# Revit family: PRD_AR_WllMntdBbTps_F5SSelfClosingMixer_F5SM1012
name_source: partatom
category: Plumbing Fixtures
units: mm (PartAtom-declared; Revit-internal decimal feet)

## family parameters
Cut with Voids When Loaded = No
Enable Cutting in Views = Yes
Host = Face
Maintain Annotation Orientation = No
OmniClass Number = 23.45.55.14
OmniClass Title = Single Faucets
Part Type = Normal
Room Calculation Point = No
Round Connector Dimension = Use Diameter
Shared = No

## types (1)
- F5SM1012
    AccentColour = none
    AdjustableFlowTime = Yes
    AssetType = Fixed
    BIMObjectName = PRD_AR_WallMountedBibTaps_F5SSelfClosingMixer_F5SM1012
    BasicColour = chrome-look (glossy)
    BodyMaterial = PRD_AR_PolishedChromium_PlatedBrass
    CW Connection = Yes
    CWFU = 0
    CalculationFlowRateColdWater = 0.07 l/s
    CalculationFlowRateHotWater = 0.07 l/s
    Category = Pr_40_20_87_93, Wall-mounted bib taps
    CloseOffRating = 0.0 Pa
    Color = chrome-look (glossy)
    DN = 15 mm  [stored 0.0492126 ft]
    Default Elevation = 1219 mm
    Depressurised = No
    Description = F5S-Mix self-closing wall-mounted mixer DN 15 as single mixer with angled outlet, for sanitary facilities, for concealed mounting. Especially suitable for facilities at risk of vandalism. FRAMIC self-closing mixer cartridge, hydraulically controlled, low-maintenance and stagnation-free, with ceramic disc technology, self-closing, flow pressure-independent due to medium separated design. Stepless adjustment of flow duration. With adjustable and turn-proof temperature stop with backflow preventers and strainers. For connection to hot and cold water. All-metal construction, polished, chromium-plated brass. Anti-theft aerator with integrated flow regulator 6.0 l/min. Connecting flange with overlapping wall bushings for wall thicknesses from 50 to 240 mm.
    DiameterNominal = DN 15
    Export Type to IFC As = IfcValveType
    FaucetFunction = MIXED
    FaucetOperation = SELFCLOSING
    FaucetTopDescription = Top section, ceramic
    FaucetType = BIB
    Features = For connection to hot and cold water. All-metal construction, polished, chromium-plated brass. Anti-theft aerator with integrated flow regulator 6.0 l/min. Other wall thicknesses on request.
    Finish = chromed
    FlowCoefficient = 0
    FlowColdWater = 0.1 L/s
    FlowHotWater = 0.1 L/s
    FunctionalPrinciple = hydraulic self-closing
    HW Connection = Yes
    HWFU = 0
    HygieneFlushing = No
    IfcExportAs = IfcValveType
    IfcExportType = FAUCET
    InletSize = G 1/2 B
    LockingMechanism = Top section, ceramic
    Manufacturer = KWC Group Management AG
    ManufacturerName = KWC Group Management AG
    ManufacturerURL = www.kwc-professional.com
    Material = polished, chromium-plated brass
    MaterialFitting = brass-look
    MaximumFlowTime = 35 Seconds
    MinimumFlowPressure = 1 bar
    MinimumFlowTime = 5 Seconds
    Model = F5SM1012
    ModelNumber = 2030071618
    ModelReference = F5SM1012
    NBSDescription = Taps and water supply fittings for sinks
    NBSReference = 45-35-70/345
    Name = F5S Self-closing mixer F5SM1012
    NominalDepth = 232 mm  [stored 0.761155 ft]
    NominalHeight = 0 mm  [stored 0 ft]
    NominalWidth = 71 mm  [stored 0.23294 ft]
    ProductInformation = http://pim.kwc.com
    Protective Shutdown = No
    Size = 15
    SoundInsulation = No
    Spout = fixed
    SpoutProjection = 170 mm
    Status = New
    SurfaceFinishFitting = chromed
    SurfaceTreatmentFitting = polished
    TemperatureLimit = Yes
    TestPressure = 0.0 Pa
    ThermalDisinfection = No
    Type IFC Predefined Type = FAUCET
    TypeOfMixing = Yes
    TypeOfMounting = concealed
    TypeOfOperation = manual operation
    TypeOfTap = bib tap
    URL = www.kwc-professional.com
    Uniclass2015Code = Pr_40_20_87_93
    Uniclass2015Title = Wall-mounted bib taps
    Uniclass2015Version = Products v1.36
    ValveMechanism = OTHER
    ValveOperation = HYDRAULIC
    ValvePattern = OTHER
    Vent Connection = Yes
    Version = 1
    VolumeFlowRateAt3Bar = 0.1 l/s
    WFU = 0
    Waste Connection = Yes
    WaterConnection = threaded connection (external)
    WithBackflowPreventer = Yes
    WithFilter = Yes
    WithRosettesCoverPlate = Yes
    WorkingPressure = 0.0 Pa

note: [stored X ft] marks values corroborated as IEEE doubles in the binary element streams (Revit-internal decimal feet)

## geometry (parser evidence)
native form markers: Sweep x5
no freeform markers — native parametric forms only
